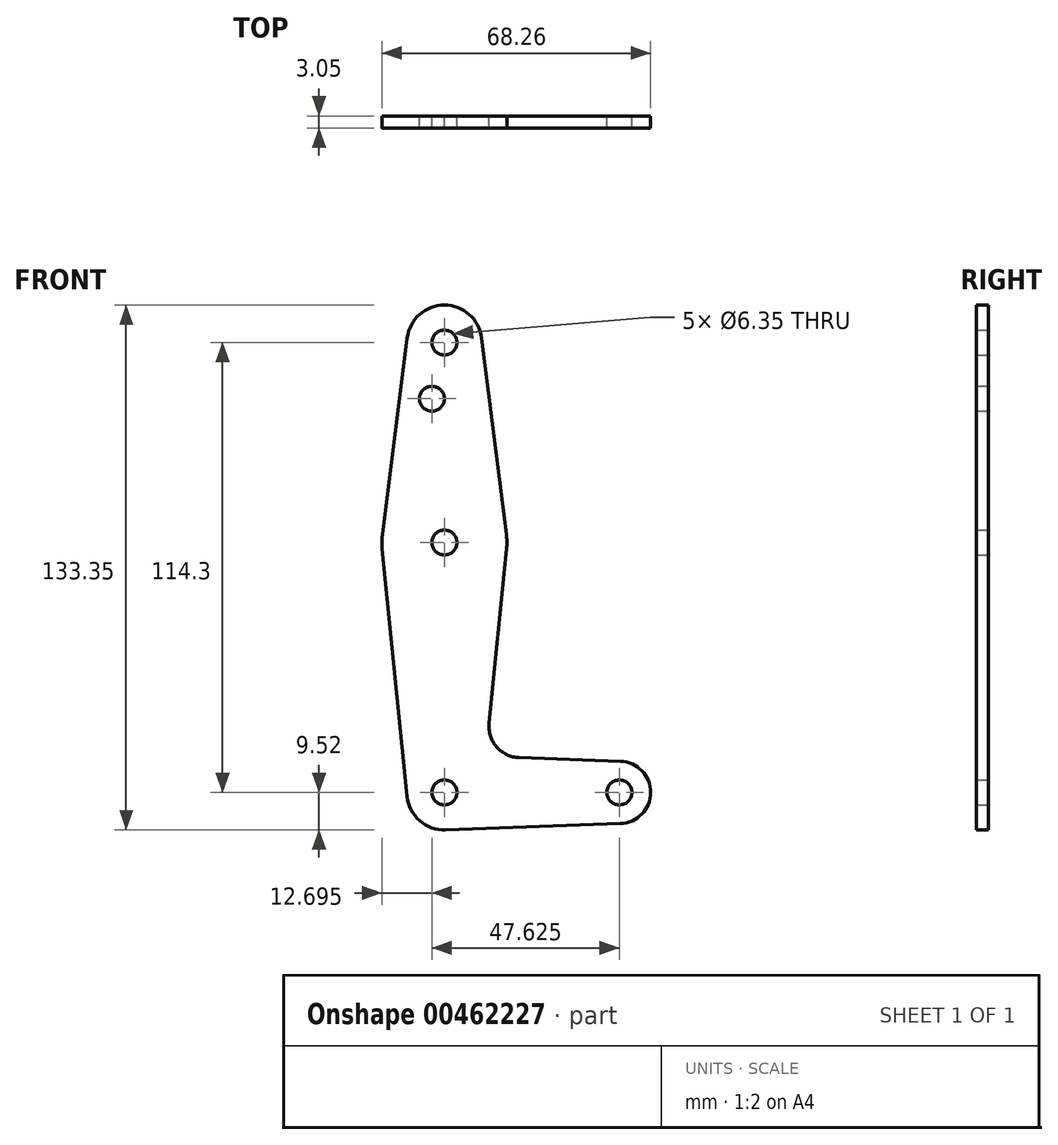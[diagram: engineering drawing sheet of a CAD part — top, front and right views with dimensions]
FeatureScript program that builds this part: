
annotation { "Feature Type Name" : "Feature", "Feature Type Description" : "" }
export const myFeature = defineFeature(function(context is Context, id is Id, definition is map)
    precondition{}
    {
        {
            var Q0;
            Q0=qCreatedBy(makeId("Front.planeOp"),FACE);
            var sketch = newSketch(context, id + "F0", { "sketchPlane" : qUnion([Q0])});
            skCircle(sketch, "E0", {"center": v(0, 0) * mm, "radius": 9.53 * mm});
            skCircle(sketch, "E1", {"center": v(0, 63.5) * mm, "radius": 15.88 * mm});
            skCircle(sketch, "E2", {"center": v(0, 114.3) * mm, "radius": 9.53 * mm});
            skCircle(sketch, "E3", {"center": v(44.45, 0) * mm, "radius": 7.94 * mm});
            skLineSegment(sketch, "E4", {"start": v(18.97, 8.85) * mm, "end": v(44.73, 7.93) * mm});
            skLineSegment(sketch, "E5.MirrorCS", {"start": v(0.34, -9.52) * mm, "end": v(44.73, -7.93) * mm});
            skLineSegment(sketch, "E6", {"start": v(11.34, 17.6) * mm, "end": v(15.8, 61.91) * mm});
            skLineSegment(sketch, "E7.MirrorCS", {"start": v(-9.48, -0.95) * mm, "end": v(-15.8, 61.91) * mm});
            skLineSegment(sketch, "E8", {"start": v(-15.75, 65.48) * mm, "end": v(-9.45, 115.5) * mm});
            skLineSegment(sketch, "E9.MirrorCS", {"start": v(15.75, 65.48) * mm, "end": v(9.45, 115.5) * mm});
            skCircle(sketch, "E10", {"center": v(0, 114.3) * mm, "radius": 3.18 * mm});
            skCircle(sketch, "E11", {"center": v(0, 63.5) * mm, "radius": 3.18 * mm});
            skCircle(sketch, "E12", {"center": v(0, 0) * mm, "radius": 3.18 * mm});
            skCircle(sketch, "E13", {"center": v(44.45, 0) * mm, "radius": 3.18 * mm});
            skCircle(sketch, "E14", {"center": v(-3.18, 100.03) * mm, "radius": 3.18 * mm});
            skArc(sketch, "E15.filletArc", {"start": v(11.34, 17.6) * mm, "mid": v(13.26, 11.57) * mm, "end": v(18.97, 8.85) * mm});
            skSolve(sketch);
        }
        {
            var Q0;
            Q0 = qSketchRegion(id + "F0", true);
            extrude(context, id + "F1", {"entities" : qUnion([Q0]), "depth" : 3.05 * mm});
        }
    });
